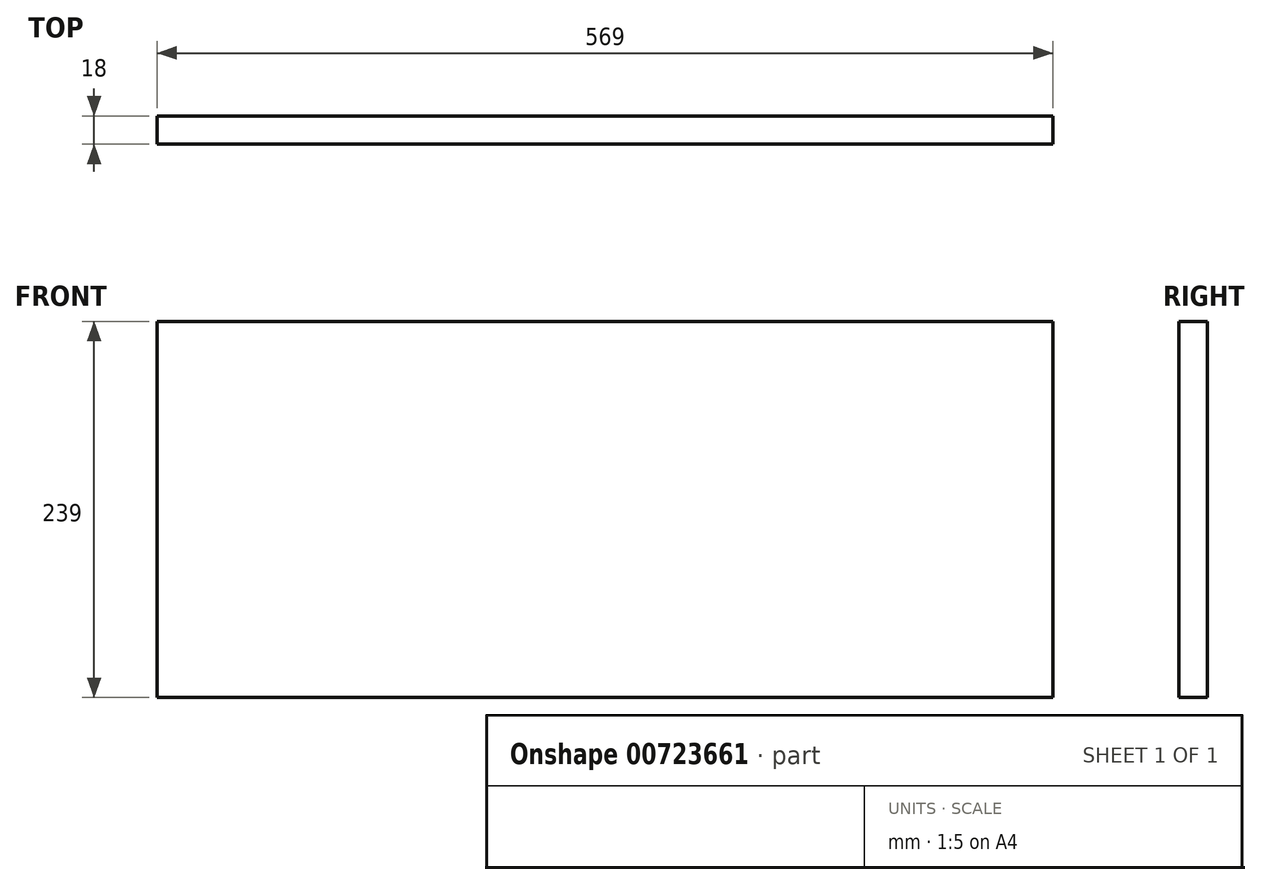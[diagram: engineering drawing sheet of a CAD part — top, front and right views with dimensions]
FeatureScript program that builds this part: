
annotation { "Feature Type Name" : "Feature", "Feature Type Description" : "" }
export const myFeature = defineFeature(function(context is Context, id is Id, definition is map)
    precondition{}
    {
        {
            var Q0;
            Q0=qCreatedBy(makeId("Front.planeOp"),FACE);
            var sketch = newSketch(context, id + "F0", { "sketchPlane" : qUnion([Q0])});
            skLineSegment(sketch, "E0.bottom", {"start": v(-284.5, 119.5) * mm, "end": v(284.5, 119.5) * mm});
            skLineSegment(sketch, "E0.top", {"start": v(-284.5, -119.5) * mm, "end": v(284.5, -119.5) * mm});
            skLineSegment(sketch, "E0.left", {"start": v(-284.5, 119.5) * mm, "end": v(-284.5, -119.5) * mm});
            skLineSegment(sketch, "E0.right", {"start": v(284.5, 119.5) * mm, "end": v(284.5, -119.5) * mm});
            skLineSegment(sketch, "E1", {"start": v(-284.5, 119.5) * mm, "end": v(284.5, -119.5) * mm, "construction": true});
            skSolve(sketch);
        }
        {
            var Q0;
            Q0 = qSketchRegion(id + "F0", true);
            extrude(context, id + "F1", {"entities" : qUnion([Q0]), "depth" : 18 * mm, "offsetDistance" : 25 * mm});
        }
    });
